# Revit family: Elevator
name_source: partatom
category: Windows
units: mm (PartAtom-declared; Revit-internal decimal feet)

## family parameters
Always vertical = Yes
Classification Number = 23.50.05.11
Cut with Voids When Loaded = No
Host = Wall
Room Calculation Point = No
Shared = No

## types (1)
- Elevator
    Assembly Code = D1010
    Carriage Height = 8' - 0"
    Carriage Material = ARCAT - Metal - Stainless Steel - 304 - Satin
    Cladding Material = ARCAT - Metal - Stainless Steel - 304 - Satin
    Construction Details = http://www.arcat.com
    Depth = 6' - 0"
    Description = Elevator
    Distance Between Floors = 10' - 0"
    Door Material = ARCAT - Metal - Stainless Steel - 304 - Satin
    Door Opening Time = 2.2 Seconds
    Drive Type = 90/120 amp AC Drive
    Expected Lifespan (Years) = 0
    Floor = 22' - 0"
    Green Building-LEED = http://www.arcat.com
    Height = 6' - 8"
    Keynote = 14200
    Maintenance Schedule (Months) = 0
    Manufacturer = Generic
    Manufacturer Fax = (203) 929-2444
    Model = Generic
    Number of Openings = 36
    Number of Stops = 36
    Power Supply = {208}{240}{440}{480}{600} VAC - 3 Phase
    Product Data = http://www.arcat.com
    Product Properties = http://www.arcat.com
    Rated Capacity_Lbs = 3000
    Roping = 2:1
    Rough Height = 31' - 2"
    Shaft Height = 40' - 0"
    Shaft Wall Construction = ARCAT - Metal - Steel 20ga - Mill
    Show Carriage on Floor = 3
    Show Door = Yes
    Show Shaft = Yes
    Specification = http://www.arcat.com
    Stopping Accuracy = 0' - 0 1/4"
    Total Floors = 4
    Travel Speed_FPM = 350
    Wall Closure = By host
    Warranty Duration (Years) = 0
    Width = 6' - 0"

## geometry (parser evidence)
native form markers: Blend x1, Sweep x5
no freeform markers — native parametric forms only
